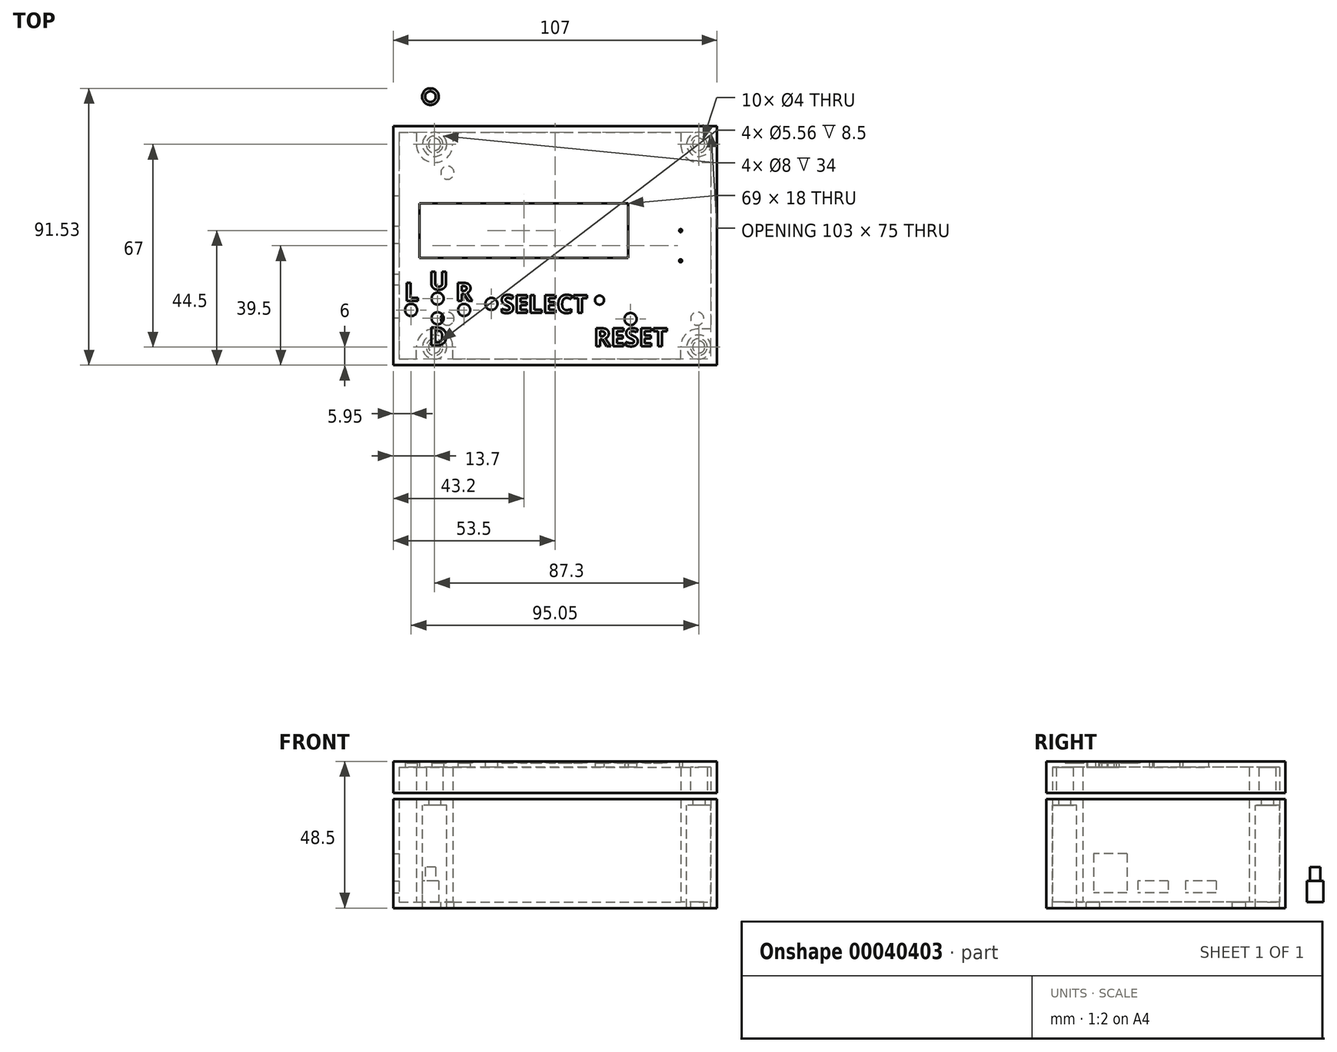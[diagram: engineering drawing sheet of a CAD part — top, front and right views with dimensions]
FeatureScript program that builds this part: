
annotation { "Feature Type Name" : "Feature", "Feature Type Description" : "" }
export const myFeature = defineFeature(function(context is Context, id is Id, definition is map)
    precondition{}
    {
        {
            assignVariable(context, id + "F0", {"name" : "Wall_T", "anyValue" : 2});
        }
        {
            var Q0;
            Q0=qCreatedBy(makeId("Top.planeOp"),FACE);
            var sketch = newSketch(context, id + "F1", { "sketchPlane" : qUnion([Q0])});
            skLineSegment(sketch, "E0.bottom", {"start": v(-50.8, 26.67) * mm, "end": v(50.8, 26.67) * mm});
            skLineSegment(sketch, "E0.top", {"start": v(-50.8, -26.67) * mm, "end": v(50.8, -26.67) * mm});
            skLineSegment(sketch, "E0.left", {"start": v(-50.8, 26.67) * mm, "end": v(-50.8, -26.67) * mm});
            skLineSegment(sketch, "E0.right", {"start": v(50.8, 26.67) * mm, "end": v(50.8, -26.67) * mm});
            skPoint(sketch, "E1", {"position": v(0, 26.67) * mm});
            skPoint(sketch, "E2", {"position": v(50.8, 0) * mm});
            skLineSegment(sketch, "E3.bottom", {"start": v(-50.8, -13.87) * mm, "end": v(-52.8, -13.87) * mm});
            skLineSegment(sketch, "E3.top", {"start": v(-50.8, -22.87) * mm, "end": v(-52.8, -22.87) * mm});
            skLineSegment(sketch, "E3.left", {"start": v(-50.8, -13.87) * mm, "end": v(-50.8, -22.87) * mm});
            skLineSegment(sketch, "E3.right", {"start": v(-52.8, -13.87) * mm, "end": v(-52.8, -22.87) * mm});
            skLineSegment(sketch, "E4.bottom", {"start": v(-50.8, -0.27) * mm, "end": v(-52.3, -0.27) * mm});
            skLineSegment(sketch, "E4.top", {"start": v(-50.8, -8.37) * mm, "end": v(-52.3, -8.37) * mm});
            skLineSegment(sketch, "E4.left", {"start": v(-50.8, -0.27) * mm, "end": v(-50.8, -8.37) * mm});
            skLineSegment(sketch, "E4.right", {"start": v(-52.3, -0.27) * mm, "end": v(-52.3, -8.37) * mm});
            skLineSegment(sketch, "E5.bottom", {"start": v(-50.8, 15.58) * mm, "end": v(-52.3, 15.58) * mm});
            skLineSegment(sketch, "E5.top", {"start": v(-50.8, 7.48) * mm, "end": v(-52.3, 7.48) * mm});
            skLineSegment(sketch, "E5.left", {"start": v(-50.8, 15.58) * mm, "end": v(-50.8, 7.48) * mm});
            skLineSegment(sketch, "E5.right", {"start": v(-52.3, 15.58) * mm, "end": v(-52.3, 7.48) * mm});
            skCircle(sketch, "E6", {"center": v(-35.56, 24.13) * mm, "radius": 0.64 * mm});
            skCircle(sketch, "E7", {"center": v(-35.56, -24.13) * mm, "radius": 0.64 * mm});
            skCircle(sketch, "E8", {"center": v(39.37, 24.13) * mm, "radius": 0.64 * mm});
            skCircle(sketch, "E9", {"center": v(15.24, 8.9) * mm, "radius": 0.64 * mm});
            skCircle(sketch, "E10", {"center": v(15.24, -19.05) * mm, "radius": 0.64 * mm});
            skCircle(sketch, "E11", {"center": v(47, -24.13) * mm, "radius": 0.64 * mm});
            skCircle(sketch, "E12", {"center": v(-44.8, 22.17) * mm, "radius": 1.5 * mm});
            skSolve(sketch);
        }
        {
            var Q0;
            Q0=qCreatedBy(makeId("Top.planeOp"),FACE);
            var sketch = newSketch(context, id + "F2", { "sketchPlane" : qUnion([Q0])});
            skLineSegment(sketch, "E13.bottom", {"start": v(-50.8, 28) * mm, "end": v(30.2, 28) * mm});
            skLineSegment(sketch, "E13.top", {"start": v(-50.8, -28) * mm, "end": v(30.2, -28) * mm});
            skLineSegment(sketch, "E13.left", {"start": v(-50.8, 28) * mm, "end": v(-50.8, -28) * mm});
            skLineSegment(sketch, "E13.right", {"start": v(30.2, 28) * mm, "end": v(30.2, -28) * mm});
            skPoint(sketch, "E14", {"position": v(30.2, 0) * mm});
            skLineSegment(sketch, "E15.bottom", {"start": v(-44.8, 14) * mm, "end": v(24.2, 14) * mm});
            skLineSegment(sketch, "E15.top", {"start": v(-44.8, -4) * mm, "end": v(24.2, -4) * mm});
            skLineSegment(sketch, "E15.left", {"start": v(-44.8, 14) * mm, "end": v(-44.8, -4) * mm});
            skLineSegment(sketch, "E15.right", {"start": v(24.2, 14) * mm, "end": v(24.2, -4) * mm});
            skCircle(sketch, "E16", {"center": v(-47.55, -21.25) * mm, "radius": 2 * mm});
            skCircle(sketch, "E17", {"center": v(-38.8, -17.5) * mm, "radius": 2 * mm});
            skCircle(sketch, "E18", {"center": v(-38.8, -24) * mm, "radius": 2 * mm});
            skCircle(sketch, "E19", {"center": v(-30.05, -21.25) * mm, "radius": 2 * mm});
            skCircle(sketch, "E20", {"center": v(-21.05, -19.25) * mm, "radius": 2 * mm});
            skCircle(sketch, "E21", {"center": v(24.95, -24.25) * mm, "radius": 2 * mm});
            skCircle(sketch, "E22", {"center": v(14.7, -18) * mm, "radius": 1.5 * mm});
            skSolve(sketch);
        }
        {
            var Q0;
            Q0=qCreatedBy(makeId("Top.planeOp"),FACE);
            var sketch = newSketch(context, id + "F3", { "sketchPlane" : qUnion([Q0])});
            skLineSegment(sketch, "E23.bottom", {"start": v(-51.5, 37.5) * mm, "end": v(51.5, 37.5) * mm});
            skLineSegment(sketch, "E23.top", {"start": v(-51.5, -37.5) * mm, "end": v(51.5, -37.5) * mm});
            skLineSegment(sketch, "E23.left", {"start": v(-51.5, 37.5) * mm, "end": v(-51.5, -37.5) * mm});
            skLineSegment(sketch, "E23.right", {"start": v(51.5, 37.5) * mm, "end": v(51.5, -37.5) * mm});
            skPoint(sketch, "E24", {"position": v(0, 37.5) * mm});
            skLineSegment(sketch, "E25.bottom", {"start": v(-53.5, 39.5) * mm, "end": v(53.5, 39.5) * mm});
            skLineSegment(sketch, "E25.top", {"start": v(-53.5, -39.5) * mm, "end": v(53.5, -39.5) * mm});
            skLineSegment(sketch, "E25.left", {"start": v(-53.5, 39.5) * mm, "end": v(-53.5, -39.5) * mm});
            skLineSegment(sketch, "E25.right", {"start": v(53.5, 39.5) * mm, "end": v(53.5, -39.5) * mm});
            skPoint(sketch, "E26", {"position": v(0, 39.5) * mm});
            skPoint(sketch, "E27", {"position": v(51.5, 0) * mm});
            skPoint(sketch, "E28", {"position": v(53.5, 0) * mm});
            skLineSegment(sketch, "E29.bottom", {"start": v(-53.5, -12.87) * mm, "end": v(-51.5, -12.87) * mm});
            skLineSegment(sketch, "E29.top", {"start": v(-53.5, -23.87) * mm, "end": v(-51.5, -23.87) * mm});
            skLineSegment(sketch, "E29.left", {"start": v(-53.5, -12.87) * mm, "end": v(-53.5, -23.87) * mm});
            skLineSegment(sketch, "E29.right", {"start": v(-51.5, -12.87) * mm, "end": v(-51.5, -23.87) * mm});
            skLineSegment(sketch, "E30.bottom", {"start": v(-53.5, 0.73) * mm, "end": v(-51.5, 0.73) * mm});
            skLineSegment(sketch, "E30.top", {"start": v(-53.5, -9.37) * mm, "end": v(-51.5, -9.37) * mm});
            skLineSegment(sketch, "E30.left", {"start": v(-53.5, 0.73) * mm, "end": v(-53.5, -9.37) * mm});
            skLineSegment(sketch, "E30.right", {"start": v(-51.5, 0.73) * mm, "end": v(-51.5, -9.37) * mm});
            skLineSegment(sketch, "E31.bottom", {"start": v(-53.5, 16.58) * mm, "end": v(-51.5, 16.58) * mm});
            skLineSegment(sketch, "E31.top", {"start": v(-53.5, 6.48) * mm, "end": v(-51.5, 6.48) * mm});
            skLineSegment(sketch, "E31.left", {"start": v(-53.5, 16.58) * mm, "end": v(-53.5, 6.48) * mm});
            skLineSegment(sketch, "E31.right", {"start": v(-51.5, 16.58) * mm, "end": v(-51.5, 6.48) * mm});
            skCircle(sketch, "E32", {"center": v(-35.56, -24.13) * mm, "radius": 2.18 * mm});
            skCircle(sketch, "E33", {"center": v(-35.56, 24.13) * mm, "radius": 2.18 * mm});
            skCircle(sketch, "E34", {"center": v(47, -24.13) * mm, "radius": 2.18 * mm});
            skCircle(sketch, "E35", {"center": v(47.5, 33.5) * mm, "radius": 4 * mm});
            skArc(sketch, "E36", {"start": v(41.5, 33.5) * mm, "mid": v(43.26, 29.26) * mm, "end": v(47.5, 27.5) * mm});
            skLineSegment(sketch, "E37", {"start": v(41.5, 33.5) * mm, "end": v(47.5, 33.5) * mm, "construction": true});
            skLineSegment(sketch, "E38", {"start": v(47.5, 27.5) * mm, "end": v(47.5, 33.5) * mm, "construction": true});
            skLineSegment(sketch, "E39", {"start": v(41.5, 33.5) * mm, "end": v(41.5, 37.5) * mm});
            skLineSegment(sketch, "E40", {"start": v(47.5, 27.5) * mm, "end": v(51.5, 27.5) * mm});
            skArc(sketch, "E41", {"start": v(47.5, -27.5) * mm, "mid": v(43.26, -29.26) * mm, "end": v(41.5, -33.5) * mm});
            skCircle(sketch, "E42", {"center": v(47.5, -33.5) * mm, "radius": 4 * mm});
            skLineSegment(sketch, "E43", {"start": v(47.5, -27.5) * mm, "end": v(51.5, -27.5) * mm});
            skLineSegment(sketch, "E44", {"start": v(47.5, -27.5) * mm, "end": v(47.5, -33.5) * mm, "construction": true});
            skLineSegment(sketch, "E45", {"start": v(41.5, -33.5) * mm, "end": v(47.5, -33.5) * mm, "construction": true});
            skLineSegment(sketch, "E46", {"start": v(41.5, -33.5) * mm, "end": v(41.5, -37.5) * mm});
            skCircle(sketch, "E47", {"center": v(-39.8, -33.5) * mm, "radius": 4 * mm});
            skArc(sketch, "E48", {"start": v(-33.8, -33.5) * mm, "mid": v(-39.8, -27.5) * mm, "end": v(-45.8, -33.5) * mm});
            skLineSegment(sketch, "E49", {"start": v(-45.8, -33.5) * mm, "end": v(-39.8, -33.5) * mm, "construction": true});
            skLineSegment(sketch, "E50", {"start": v(-33.8, -33.5) * mm, "end": v(-39.8, -33.5) * mm, "construction": true});
            skLineSegment(sketch, "E51", {"start": v(-33.8, -33.5) * mm, "end": v(-33.8, -37.5) * mm});
            skCircle(sketch, "E52", {"center": v(-39.8, 33.5) * mm, "radius": 4 * mm});
            skArc(sketch, "E53", {"start": v(-45.8, 33.5) * mm, "mid": v(-39.8, 27.5) * mm, "end": v(-33.8, 33.5) * mm});
            skLineSegment(sketch, "E54", {"start": v(-33.8, 33.5) * mm, "end": v(-39.8, 33.5) * mm, "construction": true});
            skLineSegment(sketch, "E55", {"start": v(-45.8, 33.5) * mm, "end": v(-39.8, 33.5) * mm, "construction": true});
            skLineSegment(sketch, "E56", {"start": v(-33.8, 33.5) * mm, "end": v(-33.8, 37.5) * mm});
            skLineSegment(sketch, "E57", {"start": v(-45.8, -33.5) * mm, "end": v(-45.8, -37.5) * mm});
            skLineSegment(sketch, "E58", {"start": v(-45.8, 33.5) * mm, "end": v(-45.8, 37.5) * mm});
            skCircle(sketch, "E59", {"center": v(-39.8, 33.5) * mm, "radius": 2 * mm});
            skCircle(sketch, "E60", {"center": v(47.5, 33.5) * mm, "radius": 2 * mm});
            skCircle(sketch, "E61", {"center": v(47.5, -33.5) * mm, "radius": 2 * mm});
            skCircle(sketch, "E62", {"center": v(-39.8, -33.5) * mm, "radius": 2 * mm});
            skSolve(sketch);
        }
        {
            var Q0;
            {var subQ6=sQuery(id+"F3.wireOp",EDGE,"E23.bottom");Q0=makeQuery(id+"F3.imprint","IMPRINT",FACE,{"disambiguationData":[TD([[makeQuery(id+"F3.imprint","IMPRINT",EDGE,{"derivedFrom":subQ6}),1.0]])]});}
            var Q1;
            {var subQ1=sQuery(id+"F3.wireOp",EDGE,"E30.bottom");Q1=makeQuery(id+"F3.imprint","IMPRINT",FACE,{"disambiguationData":[TD([[makeQuery(id+"F3.imprint","IMPRINT",EDGE,{"derivedFrom":subQ1}),1.0]])]});}
            var Q2;
            {var subQ1=sQuery(id+"F3.wireOp",EDGE,"E29.bottom");Q2=makeQuery(id+"F3.imprint","IMPRINT",FACE,{"disambiguationData":[TD([[makeQuery(id+"F3.imprint","IMPRINT",EDGE,{"derivedFrom":subQ1}),1.0]])]});}
            var Q3;
            {var subQ5=sQuery(id+"F3.wireOp",EDGE,"E23.bottom");Q3=makeQuery(id+"F3.imprint","IMPRINT",FACE,{"disambiguationData":[TD([[makeQuery(id+"F3.imprint","IMPRINT",EDGE,{"derivedFrom":subQ5}),-1.0]])]});}
            var Q4;
            Q4=makeQuery(id+"F3.imprint","IMPRINT",FACE,{"disambiguationData":[TD([[makeQuery(id+"F3.imprint","IMPRINT",EDGE,{"derivedFrom":sQuery(id+"F3.wireOp",EDGE,"E31.bottom")}),-1.0]])]});
            var Q5;
            Q5=makeQuery(id+"F3.imprint","IMPRINT",FACE,{"disambiguationData":[TD([[makeQuery(id+"F3.imprint","IMPRINT",EDGE,{"derivedFrom":sQuery(id+"F3.wireOp",EDGE,"E30.bottom")}),-1.0]])]});
            var Q6;
            Q6=makeQuery(id+"F3.imprint","IMPRINT",FACE,{"disambiguationData":[TD([[makeQuery(id+"F3.imprint","IMPRINT",EDGE,{"derivedFrom":sQuery(id+"F3.wireOp",EDGE,"E29.bottom")}),-1.0]])]});
            var Q7;
            {var subQ2=sQuery(id+"F3.wireOp",EDGE,"E29.right");Q7=makeQuery(id+"F3.imprint","IMPRINT",FACE,{"disambiguationData":[TD([[makeQuery(id+"F3.imprint","IMPRINT",EDGE,{"derivedFrom":subQ2}),1.0]])]});}
            var Q8;
            {var subQ0=sQuery(id+"F3.wireOp",EDGE,"E51");Q8=makeQuery(id+"F3.imprint","IMPRINT",FACE,{"disambiguationData":[TD([[makeQuery(id+"F3.imprint","IMPRINT",EDGE,{"derivedFrom":subQ0}),-1.0]])]});}
            var Q9;
            {var subQ0=sQuery(id+"F3.wireOp",EDGE,"E57");Q9=makeQuery(id+"F3.imprint","IMPRINT",FACE,{"disambiguationData":[TD([[makeQuery(id+"F3.imprint","IMPRINT",EDGE,{"derivedFrom":subQ0}),1.0]])]});}
            var Q10;
            {var subQ1=sQuery(id+"F3.wireOp",EDGE,"e28c1a44-09c7-43ad-9793-d904d9dc9239");var subQ3=sQuery(id+"F3.wireOp",EDGE,"E23.top");var subQ5=makeQuery(id+"F3.imprint","INTERSECT",VERTEX,{"derivedFrom":[subQ3,subQ1]});Q10=makeQuery(id+"F3.imprint","IMPRINT",FACE,{"disambiguationData":[TD([[makeQuery(id+"F3.imprint","IMPRINT",EDGE,{"disambiguationData":[TD([[subQ5,-1.0]])],"derivedFrom":subQ3}),1.0]])]});}
            var Q11;
            Q11=makeQuery(id+"F3.imprint","IMPRINT",FACE,{"disambiguationData":[TD([[makeQuery(id+"F3.imprint","IMPRINT",EDGE,{"derivedFrom":sQuery(id+"F3.wireOp",EDGE,"E32")}),-1.0]])]});
            var Q12;
            {var subQ0=sQuery(id+"F3.wireOp",EDGE,"E56");Q12=makeQuery(id+"F3.imprint","IMPRINT",FACE,{"disambiguationData":[TD([[makeQuery(id+"F3.imprint","IMPRINT",EDGE,{"derivedFrom":subQ0}),1.0]])]});}
            var Q13;
            Q13=makeQuery(id+"F3.imprint","IMPRINT",FACE,{"disambiguationData":[TD([[makeQuery(id+"F3.imprint","IMPRINT",EDGE,{"derivedFrom":sQuery(id+"F3.wireOp",EDGE,"E36")}),1.0]])]});
            var Q14;
            Q14=makeQuery(id+"F3.imprint","IMPRINT",FACE,{"disambiguationData":[TD([[makeQuery(id+"F3.imprint","IMPRINT",EDGE,{"derivedFrom":sQuery(id+"F3.wireOp",EDGE,"E41")}),1.0]])]});
            var Q15;
            {var subQ1=sQuery(id+"F3.wireOp",EDGE,"E23.right");var subQ3=sQuery(id+"F3.wireOp",EDGE,"E23.top");var subQ5=makeQuery(id+"F3.imprint","INTERSECT",VERTEX,{"derivedFrom":[subQ3,subQ1]});Q15=makeQuery(id+"F3.imprint","IMPRINT",FACE,{"disambiguationData":[TD([[makeQuery(id+"F3.imprint","IMPRINT",EDGE,{"disambiguationData":[TD([[subQ5,1.0]])],"derivedFrom":subQ3}),1.0]])]});}
            var Q16;
            {var subQ0=sQuery(id+"F3.wireOp",EDGE,"E58");Q16=makeQuery(id+"F3.imprint","IMPRINT",FACE,{"disambiguationData":[TD([[makeQuery(id+"F3.imprint","IMPRINT",EDGE,{"derivedFrom":subQ0}),-1.0]])]});}
            var Q17;
            {var subQ0=sQuery(id+"F3.wireOp",EDGE,"E23.right");var subQ1=sQuery(id+"F3.wireOp",EDGE,"E23.bottom");var subQ2=makeQuery(id+"F3.imprint","INTERSECT",VERTEX,{"derivedFrom":[subQ1,subQ0]});Q17=makeQuery(id+"F3.imprint","IMPRINT",FACE,{"disambiguationData":[TD([[makeQuery(id+"F3.imprint","IMPRINT",EDGE,{"disambiguationData":[TD([[subQ2,1.0]])],"derivedFrom":subQ1}),-1.0]])]});}
            extrude(context, id + "F4", {"entities" : qUnion([Q0, Q1, Q2, Q3, Q4, Q5, Q6, Q7, Q8, Q9, Q10, Q11, Q12, Q13, Q14, Q15, Q16, Q17]), "oppositeDirection" : true, "depth" : (getVariable(context, 'Wall_T')) * mm});
        }
        {
            var Q0;
            {var subQ30=sQuery(id+"F3.wireOp",EDGE,"E25.bottom");Q0=makeQuery(id+"F3.imprint","IMPRINT",FACE,{"disambiguationData":[TD([[makeQuery(id+"F3.imprint","IMPRINT",EDGE,{"derivedFrom":subQ30}),-1.0]])]});}
            var Q1;
            {var subQ1=sQuery(id+"F3.wireOp",EDGE,"E29.bottom");Q1=makeQuery(id+"F3.imprint","IMPRINT",FACE,{"disambiguationData":[TD([[makeQuery(id+"F3.imprint","IMPRINT",EDGE,{"derivedFrom":subQ1}),1.0]])]});}
            var Q2;
            {var subQ1=sQuery(id+"F3.wireOp",EDGE,"E30.bottom");Q2=makeQuery(id+"F3.imprint","IMPRINT",FACE,{"disambiguationData":[TD([[makeQuery(id+"F3.imprint","IMPRINT",EDGE,{"derivedFrom":subQ1}),1.0]])]});}
            var Q3;
            {var subQ0=sQuery(id+"F3.wireOp",EDGE,"E58");Q3=makeQuery(id+"F3.imprint","IMPRINT",FACE,{"disambiguationData":[TD([[makeQuery(id+"F3.imprint","IMPRINT",EDGE,{"derivedFrom":subQ0}),-1.0]])]});}
            var Q4;
            {var subQ1=sQuery(id+"F3.wireOp",EDGE,"e28c1a44-09c7-43ad-9793-d904d9dc9239");var subQ3=sQuery(id+"F3.wireOp",EDGE,"E23.bottom");var subQ5=makeQuery(id+"F3.imprint","INTERSECT",VERTEX,{"derivedFrom":[subQ3,subQ1]});Q4=makeQuery(id+"F3.imprint","IMPRINT",FACE,{"disambiguationData":[TD([[makeQuery(id+"F3.imprint","IMPRINT",EDGE,{"disambiguationData":[TD([[subQ5,-1.0]])],"derivedFrom":subQ3}),-1.0]])]});}
            var Q5;
            {var subQ0=sQuery(id+"F3.wireOp",EDGE,"E56");Q5=makeQuery(id+"F3.imprint","IMPRINT",FACE,{"disambiguationData":[TD([[makeQuery(id+"F3.imprint","IMPRINT",EDGE,{"derivedFrom":subQ0}),1.0]])]});}
            var Q6;
            Q6=makeQuery(id+"F3.imprint","IMPRINT",FACE,{"disambiguationData":[TD([[makeQuery(id+"F3.imprint","IMPRINT",EDGE,{"derivedFrom":sQuery(id+"F3.wireOp",EDGE,"E36")}),1.0]])]});
            var Q7;
            {var subQ1=sQuery(id+"F3.wireOp",EDGE,"E23.right");var subQ3=sQuery(id+"F3.wireOp",EDGE,"E23.bottom");var subQ5=makeQuery(id+"F3.imprint","INTERSECT",VERTEX,{"derivedFrom":[subQ3,subQ1]});Q7=makeQuery(id+"F3.imprint","IMPRINT",FACE,{"disambiguationData":[TD([[makeQuery(id+"F3.imprint","IMPRINT",EDGE,{"disambiguationData":[TD([[subQ5,1.0]])],"derivedFrom":subQ3}),-1.0]])]});}
            var Q8;
            {var subQ0=sQuery(id+"F3.wireOp",EDGE,"E51");Q8=makeQuery(id+"F3.imprint","IMPRINT",FACE,{"disambiguationData":[TD([[makeQuery(id+"F3.imprint","IMPRINT",EDGE,{"derivedFrom":subQ0}),-1.0]])]});}
            var Q9;
            {var subQ1=sQuery(id+"F3.wireOp",EDGE,"e28c1a44-09c7-43ad-9793-d904d9dc9239");var subQ3=sQuery(id+"F3.wireOp",EDGE,"E23.top");var subQ5=makeQuery(id+"F3.imprint","INTERSECT",VERTEX,{"derivedFrom":[subQ3,subQ1]});Q9=makeQuery(id+"F3.imprint","IMPRINT",FACE,{"disambiguationData":[TD([[makeQuery(id+"F3.imprint","IMPRINT",EDGE,{"disambiguationData":[TD([[subQ5,-1.0]])],"derivedFrom":subQ3}),1.0]])]});}
            var Q10;
            {var subQ0=sQuery(id+"F3.wireOp",EDGE,"E57");Q10=makeQuery(id+"F3.imprint","IMPRINT",FACE,{"disambiguationData":[TD([[makeQuery(id+"F3.imprint","IMPRINT",EDGE,{"derivedFrom":subQ0}),1.0]])]});}
            var Q11;
            {var subQ1=sQuery(id+"F3.wireOp",EDGE,"E23.right");var subQ3=sQuery(id+"F3.wireOp",EDGE,"E23.top");var subQ5=makeQuery(id+"F3.imprint","INTERSECT",VERTEX,{"derivedFrom":[subQ3,subQ1]});Q11=makeQuery(id+"F3.imprint","IMPRINT",FACE,{"disambiguationData":[TD([[makeQuery(id+"F3.imprint","IMPRINT",EDGE,{"disambiguationData":[TD([[subQ5,1.0]])],"derivedFrom":subQ3}),1.0]])]});}
            var Q12;
            Q12=makeQuery(id+"F3.imprint","IMPRINT",FACE,{"disambiguationData":[TD([[makeQuery(id+"F3.imprint","IMPRINT",EDGE,{"derivedFrom":sQuery(id+"F3.wireOp",EDGE,"E41")}),1.0]])]});
            var Q13;
            Q13=makeQuery(id+"F3.imprint","IMPRINT",FACE,{"disambiguationData":[TD([[makeQuery(id+"F3.imprint","IMPRINT",EDGE,{"derivedFrom":sQuery(id+"F3.wireOp",EDGE,"E31.bottom")}),-1.0]])]});
            var Q14;
            Q14=makeQuery(id+"F3.imprint","IMPRINT",FACE,{"disambiguationData":[TD([[makeQuery(id+"F3.imprint","IMPRINT",EDGE,{"derivedFrom":sQuery(id+"F3.wireOp",EDGE,"E30.bottom")}),-1.0]])]});
            var Q15;
            Q15=makeQuery(id+"F3.imprint","IMPRINT",FACE,{"disambiguationData":[TD([[makeQuery(id+"F3.imprint","IMPRINT",EDGE,{"derivedFrom":sQuery(id+"F3.wireOp",EDGE,"E29.bottom")}),-1.0]])]});
            extrude(context, id + "F5", {"entities" : qUnion([Q0, Q1, Q2, Q3, Q4, Q5, Q6, Q7, Q8, Q9, Q10, Q11, Q12, Q13, Q14, Q15]), "operationType" : NewBodyOperationType.ADD, "depth" : 34 * mm});
        }
        {
            var Q0;
            Q0=makeQuery(id+"F3.imprint","IMPRINT",FACE,{"disambiguationData":[TD([[makeQuery(id+"F3.imprint","IMPRINT",EDGE,{"derivedFrom":sQuery(id+"F3.wireOp",EDGE,"E31.bottom")}),-1.0]])]});
            var Q1;
            Q1=makeQuery(id+"F3.imprint","IMPRINT",FACE,{"disambiguationData":[TD([[makeQuery(id+"F3.imprint","IMPRINT",EDGE,{"derivedFrom":sQuery(id+"F3.wireOp",EDGE,"E30.bottom")}),-1.0]])]});
            extrude(context, id + "F6", {"entities" : qUnion([Q0, Q1]), "operationType" : NewBodyOperationType.REMOVE, "depth" : 7 * mm, "hasSecondDirection" : true, "secondDirectionOppositeDirection" : false, "secondDirectionDepth" : 3 * mm});
        }
        {
            var Q0;
            Q0=makeQuery(id+"F3.imprint","IMPRINT",FACE,{"disambiguationData":[TD([[makeQuery(id+"F3.imprint","IMPRINT",EDGE,{"derivedFrom":sQuery(id+"F3.wireOp",EDGE,"E29.bottom")}),-1.0]])]});
            var Q1;
            Q1=makeQuery(id+"F6.opExtrude","CAP_FACE",FACE,{"disambiguationData":[OSD([sQuery(id+"F3.wireOp",EDGE,"E31.bottom"),sQuery(id+"F3.wireOp",EDGE,"E31.top"),sQuery(id+"F3.wireOp",EDGE,"E31.left"),sQuery(id+"F3.wireOp",EDGE,"E31.right")])],"isStart":false});
            var Q2;
            {var subQ0=sQuery(id+"F3.wireOp",EDGE,"E23.bottom");var subQ1=sQuery(id+"F3.wireOp",EDGE,"E23.top");var subQ2=sQuery(id+"F3.wireOp",EDGE,"E25.bottom");var subQ3=sQuery(id+"F3.wireOp",EDGE,"E25.top");var subQ4=sQuery(id+"F3.wireOp",EDGE,"E25.left");var subQ5=sQuery(id+"F3.wireOp",EDGE,"E29.left");var subQ6=sQuery(id+"F3.wireOp",EDGE,"E30.left");var subQ7=sQuery(id+"F3.wireOp",EDGE,"E31.left");var subQ8=sQuery(id+"F3.wireOp",EDGE,"e28c1a44-09c7-43ad-9793-d904d9dc9239");var subQ9=sQuery(id+"F3.wireOp",EDGE,"E48");var subQ10=sQuery(id+"F3.wireOp",EDGE,"E53");var subQ17=sQuery(id+"F3.wireOp",EDGE,"E29.bottom");Q2=makeQuery(id+"FmseZqoOlNMf1UM_2.boolean.opBoolean","SPLIT",FACE,{"disambiguationData":[TD([makeQuery(id+"F5.opExtrude","SWEPT_FACE",FACE,{"disambiguationData":[OSD([subQ17])]})])],"derivedFrom":makeQuery(id+"FmseZqoOlNMf1UM_2.opExtrude","CAP_FACE",FACE,{"disambiguationData":[OSD([subQ0,subQ1,sQuery(id+"F3.wireOp",EDGE,"E23.right"),subQ2,subQ3,subQ4,sQuery(id+"F3.wireOp",EDGE,"E25.right"),subQ5,subQ6,subQ7,subQ8,sQuery(id+"F3.wireOp",EDGE,"E36"),sQuery(id+"F3.wireOp",EDGE,"E39"),sQuery(id+"F3.wireOp",EDGE,"E40"),sQuery(id+"F3.wireOp",EDGE,"E41"),sQuery(id+"F3.wireOp",EDGE,"E43"),sQuery(id+"F3.wireOp",EDGE,"E46"),subQ9,sQuery(id+"F3.wireOp",EDGE,"E51"),subQ10,sQuery(id+"F3.wireOp",EDGE,"E56"),sQuery(id+"F3.wireOp",EDGE,"E59"),sQuery(id+"F3.wireOp",EDGE,"E60"),sQuery(id+"F3.wireOp",EDGE,"E61"),sQuery(id+"F3.wireOp",EDGE,"E62")])],"isStart":true})});}
            extrude(context, id + "F7", {"entities" : qUnion([Q0]), "operationType" : NewBodyOperationType.REMOVE, "endBoundEntityFace" : qUnion([Q1]), "depth" : 16 * mm, "hasSecondDirection" : true, "secondDirectionOppositeDirection" : false, "secondDirectionBoundEntityFace" : qUnion([Q2]), "secondDirectionDepth" : 3 * mm});
        }
        {
            var Q0;
            Q0=makeQuery(id+"F3.imprint","IMPRINT",FACE,{"disambiguationData":[TD([[makeQuery(id+"F3.imprint","IMPRINT",EDGE,{"derivedFrom":sQuery(id+"F3.wireOp",EDGE,"E52")}),1.0]])]});
            var Q1;
            Q1=makeQuery(id+"F3.imprint","IMPRINT",FACE,{"disambiguationData":[TD([[makeQuery(id+"F3.imprint","IMPRINT",EDGE,{"derivedFrom":sQuery(id+"F3.wireOp",EDGE,"E47")}),1.0]])]});
            var Q2;
            Q2=makeQuery(id+"F3.imprint","IMPRINT",FACE,{"disambiguationData":[TD([[makeQuery(id+"F3.imprint","IMPRINT",EDGE,{"derivedFrom":sQuery(id+"F3.wireOp",EDGE,"E60")}),-1.0]])]});
            var Q3;
            Q3=makeQuery(id+"F3.imprint","IMPRINT",FACE,{"disambiguationData":[TD([[makeQuery(id+"F3.imprint","IMPRINT",EDGE,{"derivedFrom":sQuery(id+"F3.wireOp",EDGE,"E61")}),-1.0]])]});
            extrude(context, id + "F8", {"entities" : qUnion([Q0, Q1, Q2, Q3]), "operationType" : NewBodyOperationType.ADD, "depth" : 34 * mm, "hasSecondDirection" : true, "secondDirectionOppositeDirection" : false, "secondDirectionDepth" : 32 * mm});
        }
        {
            var Q0;
            Q0=qCreatedBy(makeId("Top.planeOp"),FACE);
            var sketch = newSketch(context, id + "F9", { "sketchPlane" : qUnion([Q0])});
            skCircle(sketch, "E63", {"center": v(41.5, 5) * mm, "radius": 0.5 * mm});
            skCircle(sketch, "E64", {"center": v(41.5, -5) * mm, "radius": 0.5 * mm});
            skLineSegment(sketch, "E65.bottom", {"start": v(-51.5, 37.5) * mm, "end": v(51.5, 37.5) * mm});
            skLineSegment(sketch, "E65.top", {"start": v(-51.5, -37.5) * mm, "end": v(51.5, -37.5) * mm});
            skLineSegment(sketch, "E65.left", {"start": v(-51.5, 37.5) * mm, "end": v(-51.5, -37.5) * mm});
            skLineSegment(sketch, "E65.right", {"start": v(51.5, 37.5) * mm, "end": v(51.5, -37.5) * mm});
            skLineSegment(sketch, "E66.bottom", {"start": v(-53.5, 39.5) * mm, "end": v(53.5, 39.5) * mm});
            skLineSegment(sketch, "E66.top", {"start": v(-53.5, -39.5) * mm, "end": v(53.5, -39.5) * mm});
            skLineSegment(sketch, "E66.left", {"start": v(-53.5, 39.5) * mm, "end": v(-53.5, -39.5) * mm});
            skLineSegment(sketch, "E66.right", {"start": v(53.5, 39.5) * mm, "end": v(53.5, -39.5) * mm});
            skLineSegment(sketch, "E67", {"start": v(41.5, 5) * mm, "end": v(41.5, -5) * mm, "construction": true});
            skPoint(sketch, "E68", {"position": v(41.5, 0) * mm});
            skCircle(sketch, "E69", {"center": v(-39.8, 33.5) * mm, "radius": 2.78 * mm});
            skLineSegment(sketch, "E70", {"start": v(-45.8, 37.5) * mm, "end": v(-45.8, 33.5) * mm});
            skLineSegment(sketch, "E71", {"start": v(-33.8, 37.5) * mm, "end": v(-33.8, 33.5) * mm});
            skArc(sketch, "E72", {"start": v(-45.8, 33.5) * mm, "mid": v(-39.8, 27.5) * mm, "end": v(-33.8, 33.5) * mm});
            skLineSegment(sketch, "E73", {"start": v(41.5, 37.5) * mm, "end": v(41.5, 33.5) * mm});
            skLineSegment(sketch, "E74", {"start": v(51.5, 27.5) * mm, "end": v(47.5, 27.5) * mm});
            skLineSegment(sketch, "E75", {"start": v(51.5, -27.5) * mm, "end": v(47.5, -27.5) * mm});
            skLineSegment(sketch, "E76", {"start": v(41.5, -37.5) * mm, "end": v(41.5, -33.5) * mm});
            skLineSegment(sketch, "E77", {"start": v(-33.8, -37.5) * mm, "end": v(-33.8, -33.5) * mm});
            skLineSegment(sketch, "E78", {"start": v(-45.8, -37.5) * mm, "end": v(-45.8, -33.5) * mm});
            skArc(sketch, "E79", {"start": v(41.5, 33.5) * mm, "mid": v(43.26, 29.26) * mm, "end": v(47.5, 27.5) * mm});
            skArc(sketch, "E80", {"start": v(41.5, -33.5) * mm, "mid": v(43.26, -29.26) * mm, "end": v(47.5, -27.5) * mm});
            skArc(sketch, "E81", {"start": v(-45.8, -33.5) * mm, "mid": v(-39.8, -27.5) * mm, "end": v(-33.8, -33.5) * mm});
            skCircle(sketch, "E82", {"center": v(47.5, 33.5) * mm, "radius": 2.78 * mm});
            skCircle(sketch, "E83", {"center": v(47.5, -33.5) * mm, "radius": 2.78 * mm});
            skCircle(sketch, "E84", {"center": v(-39.8, -33.5) * mm, "radius": 2.78 * mm});
            skText(sketch, "E85", { "text": "RESET", "fontName": "OpenSans-Bold.ttf"});
            skText(sketch, "E86", { "text": "SELECT", "fontName": "OpenSans-Bold.ttf"});
            skPoint(sketch, "E87", {"position": v(-18.05, -19.25) * mm});
            skText(sketch, "E88", { "text": "U", "fontName": "OpenSans-Bold.ttf"});
            skText(sketch, "E89", { "text": "D", "fontName": "OpenSans-Bold.ttf"});
            skText(sketch, "E90", { "text": "L", "fontName": "OpenSans-Bold.ttf"});
            skText(sketch, "E91", { "text": "R", "fontName": "OpenSans-Bold.ttf"});
            const initialGuessF9  = {"E85": [0.0129, -0.03325, 1, 0, 0.006], "E86": [-0.01805, -0.02225, 1, 0, 0.006], "E88": [-0.0416, -0.0145, 1, 0, 0.006], "E89": [-0.04164, -0.033, 1, 0, 0.006], "E90": [-0.04976, -0.01825, 1, 0, 0.006], "E91": [-0.0328, -0.01825, 1, 0, 0.006]};
            skSetInitialGuess(sketch, initialGuessF9);
            skSolve(sketch);
        }
        {
            var Q0;
            Q0=makeQuery(id+"F9.imprint","IMPRINT",FACE,{"disambiguationData":[TD([[makeQuery(id+"F9.imprint","IMPRINT",EDGE,{"derivedFrom":sQuery(id+"F9.wireOp",EDGE,"E88.sketch_text.stroke-0")}),-1.0]])]});
            var Q1;
            Q1=makeQuery(id+"F9.imprint","IMPRINT",FACE,{"disambiguationData":[TD([[makeQuery(id+"F9.imprint","IMPRINT",EDGE,{"derivedFrom":sQuery(id+"F9.wireOp",EDGE,"E90.sketch_text.stroke-0")}),-1.0]])]});
            var Q2;
            Q2=makeQuery(id+"F9.imprint","IMPRINT",FACE,{"disambiguationData":[TD([[makeQuery(id+"F9.imprint","IMPRINT",EDGE,{"derivedFrom":sQuery(id+"F9.wireOp",EDGE,"E91.sketch_text.stroke-0")}),-1.0]])]});
            var Q3;
            Q3=makeQuery(id+"F9.imprint","IMPRINT",FACE,{"disambiguationData":[TD([[makeQuery(id+"F9.imprint","IMPRINT",EDGE,{"derivedFrom":sQuery(id+"F9.wireOp",EDGE,"E63")}),-1.0]])]});
            var Q4;
            Q4=makeQuery(id+"F9.imprint","IMPRINT",FACE,{"disambiguationData":[TD([[makeQuery(id+"F9.imprint","IMPRINT",EDGE,{"derivedFrom":sQuery(id+"F9.wireOp",EDGE,"E91.sketch_text.stroke-0")}),1.0]])]});
            var Q5;
            Q5=makeQuery(id+"F9.imprint","IMPRINT",FACE,{"disambiguationData":[TD([[makeQuery(id+"F9.imprint","IMPRINT",EDGE,{"derivedFrom":sQuery(id+"F9.wireOp",EDGE,"E86.sketch_text.stroke-0")}),-1.0]])]});
            var Q6;
            Q6=makeQuery(id+"F9.imprint","IMPRINT",FACE,{"disambiguationData":[TD([[makeQuery(id+"F9.imprint","IMPRINT",EDGE,{"derivedFrom":sQuery(id+"F9.wireOp",EDGE,"E86.sketch_text.stroke-28")}),-1.0]])]});
            var Q7;
            Q7=makeQuery(id+"F9.imprint","IMPRINT",FACE,{"disambiguationData":[TD([[makeQuery(id+"F9.imprint","IMPRINT",EDGE,{"derivedFrom":sQuery(id+"F9.wireOp",EDGE,"E86.sketch_text.stroke-40")}),-1.0]])]});
            var Q8;
            Q8=makeQuery(id+"F9.imprint","IMPRINT",FACE,{"disambiguationData":[TD([[makeQuery(id+"F9.imprint","IMPRINT",EDGE,{"derivedFrom":sQuery(id+"F9.wireOp",EDGE,"E86.sketch_text.stroke-46")}),-1.0]])]});
            var Q9;
            Q9=makeQuery(id+"F9.imprint","IMPRINT",FACE,{"disambiguationData":[TD([[makeQuery(id+"F9.imprint","IMPRINT",EDGE,{"derivedFrom":sQuery(id+"F9.wireOp",EDGE,"E86.sketch_text.stroke-58")}),-1.0]])]});
            var Q10;
            Q10=makeQuery(id+"F9.imprint","IMPRINT",FACE,{"disambiguationData":[TD([[makeQuery(id+"F9.imprint","IMPRINT",EDGE,{"derivedFrom":sQuery(id+"F9.wireOp",EDGE,"E86.sketch_text.stroke-73")}),-1.0]])]});
            var Q11;
            Q11=makeQuery(id+"F9.imprint","IMPRINT",FACE,{"disambiguationData":[TD([[makeQuery(id+"F9.imprint","IMPRINT",EDGE,{"derivedFrom":sQuery(id+"F9.wireOp",EDGE,"E85.sketch_text.stroke-0")}),1.0]])]});
            var Q12;
            Q12=makeQuery(id+"F9.imprint","IMPRINT",FACE,{"disambiguationData":[TD([[makeQuery(id+"F9.imprint","IMPRINT",EDGE,{"derivedFrom":sQuery(id+"F9.wireOp",EDGE,"E85.sketch_text.stroke-0")}),-1.0]])]});
            var Q13;
            Q13=makeQuery(id+"F9.imprint","IMPRINT",FACE,{"disambiguationData":[TD([[makeQuery(id+"F9.imprint","IMPRINT",EDGE,{"derivedFrom":sQuery(id+"F9.wireOp",EDGE,"E85.sketch_text.stroke-19")}),-1.0]])]});
            var Q14;
            Q14=makeQuery(id+"F9.imprint","IMPRINT",FACE,{"disambiguationData":[TD([[makeQuery(id+"F9.imprint","IMPRINT",EDGE,{"derivedFrom":sQuery(id+"F9.wireOp",EDGE,"E85.sketch_text.stroke-31")}),-1.0]])]});
            var Q15;
            Q15=makeQuery(id+"F9.imprint","IMPRINT",FACE,{"disambiguationData":[TD([[makeQuery(id+"F9.imprint","IMPRINT",EDGE,{"derivedFrom":sQuery(id+"F9.wireOp",EDGE,"E85.sketch_text.stroke-59")}),-1.0]])]});
            var Q16;
            Q16=makeQuery(id+"F9.imprint","IMPRINT",FACE,{"disambiguationData":[TD([[makeQuery(id+"F9.imprint","IMPRINT",EDGE,{"derivedFrom":sQuery(id+"F9.wireOp",EDGE,"E85.sketch_text.stroke-71")}),-1.0]])]});
            var Q17;
            {var subQ1=sQuery(id+"F9.wireOp",EDGE,"E75");Q17=makeQuery(id+"F9.imprint","IMPRINT",FACE,{"disambiguationData":[TD([[makeQuery(id+"F9.imprint","IMPRINT",EDGE,{"derivedFrom":subQ1}),1.0]])]});}
            var Q18;
            Q18=makeQuery(id+"F9.imprint","IMPRINT",FACE,{"disambiguationData":[TD([[makeQuery(id+"F9.imprint","IMPRINT",EDGE,{"derivedFrom":sQuery(id+"F9.wireOp",EDGE,"E83")}),1.0]])]});
            var Q19;
            Q19=makeQuery(id+"F9.imprint","IMPRINT",FACE,{"disambiguationData":[TD([[makeQuery(id+"F9.imprint","IMPRINT",EDGE,{"derivedFrom":sQuery(id+"F9.wireOp",EDGE,"E69")}),1.0]])]});
            var Q20;
            Q20=makeQuery(id+"F9.imprint","IMPRINT",FACE,{"disambiguationData":[TD([[makeQuery(id+"F9.imprint","IMPRINT",EDGE,{"derivedFrom":sQuery(id+"F9.wireOp",EDGE,"E69")}),-1.0]])]});
            var Q21;
            {var subQ7=sQuery(id+"F9.wireOp",EDGE,"E65.left");Q21=makeQuery(id+"F9.imprint","IMPRINT",FACE,{"disambiguationData":[TD([[makeQuery(id+"F9.imprint","IMPRINT",EDGE,{"derivedFrom":subQ7}),-1.0]])]});}
            var Q22;
            Q22=makeQuery(id+"F9.imprint","IMPRINT",FACE,{"disambiguationData":[TD([[makeQuery(id+"F9.imprint","IMPRINT",EDGE,{"derivedFrom":sQuery(id+"F9.wireOp",EDGE,"E82")}),1.0]])]});
            var Q23;
            {var subQ1=sQuery(id+"F9.wireOp",EDGE,"E73");Q23=makeQuery(id+"F9.imprint","IMPRINT",FACE,{"disambiguationData":[TD([[makeQuery(id+"F9.imprint","IMPRINT",EDGE,{"derivedFrom":subQ1}),1.0]])]});}
            var Q24;
            {var subQ4=sQuery(id+"F9.wireOp",EDGE,"E89.sketch_text.stroke-7");Q24=makeQuery(id+"F9.imprint","IMPRINT",FACE,{"disambiguationData":[TD([[makeQuery(id+"F9.imprint","IMPRINT",EDGE,{"derivedFrom":subQ4}),1.0]])]});}
            var Q25;
            {var subQ5=sQuery(id+"F9.wireOp",EDGE,"E89.sketch_text.stroke-10");Q25=makeQuery(id+"F9.imprint","IMPRINT",FACE,{"disambiguationData":[TD([[makeQuery(id+"F9.imprint","IMPRINT",EDGE,{"derivedFrom":subQ5}),1.0]])]});}
            var Q26;
            {var subQ0=sQuery(id+"F9.wireOp",EDGE,"E89.sketch_text.stroke-2");Q26=makeQuery(id+"F9.imprint","IMPRINT",FACE,{"disambiguationData":[TD([[makeQuery(id+"F9.imprint","IMPRINT",EDGE,{"derivedFrom":subQ0}),-1.0]])]});}
            var Q27;
            {var subQ10=sQuery(id+"F9.wireOp",EDGE,"E89.sketch_text.stroke-0");Q27=makeQuery(id+"F9.imprint","IMPRINT",FACE,{"disambiguationData":[TD([[makeQuery(id+"F9.imprint","IMPRINT",EDGE,{"derivedFrom":subQ10}),-1.0]])]});}
            var Q28;
            {var subQ1=sQuery(id+"F9.wireOp",EDGE,"E89.sketch_text.stroke-4");Q28=makeQuery(id+"F9.imprint","IMPRINT",FACE,{"disambiguationData":[TD([[makeQuery(id+"F9.imprint","IMPRINT",EDGE,{"derivedFrom":subQ1}),-1.0]])]});}
            var Q29;
            {var subQ4=sQuery(id+"F9.wireOp",EDGE,"E77");Q29=makeQuery(id+"F9.imprint","IMPRINT",FACE,{"disambiguationData":[TD([[makeQuery(id+"F9.imprint","IMPRINT",EDGE,{"derivedFrom":subQ4}),1.0]])]});}
            var Q30;
            {var subQ5=sQuery(id+"F9.wireOp",EDGE,"E89.sketch_text.stroke-2");Q30=makeQuery(id+"F9.imprint","IMPRINT",FACE,{"disambiguationData":[TD([[makeQuery(id+"F9.imprint","IMPRINT",EDGE,{"derivedFrom":subQ5}),1.0]])]});}
            extrude(context, id + "F10", {"entities" : qUnion([Q0, Q1, Q2, Q3, Q4, Q5, Q6, Q7, Q8, Q9, Q10, Q11, Q12, Q13, Q14, Q15, Q16, Q17, Q18, Q19, Q20, Q21, Q22, Q23, Q24, Q25, Q26, Q27, Q28, Q29, Q30]), "depth" : 46.5 * mm, "hasSecondDirection" : true, "secondDirectionOppositeDirection" : false, "secondDirectionDepth" : 44.5 * mm});
        }
        {
            var Q0;
            {var subQ7=sQuery(id+"F9.wireOp",EDGE,"E65.left");Q0=makeQuery(id+"F9.imprint","IMPRINT",FACE,{"disambiguationData":[TD([[makeQuery(id+"F9.imprint","IMPRINT",EDGE,{"derivedFrom":subQ7}),-1.0]])]});}
            var Q1;
            Q1=makeQuery(id+"F9.imprint","IMPRINT",FACE,{"disambiguationData":[TD([[makeQuery(id+"F9.imprint","IMPRINT",EDGE,{"derivedFrom":sQuery(id+"F9.wireOp",EDGE,"E69")}),-1.0]])]});
            var Q2;
            {var subQ1=sQuery(id+"F9.wireOp",EDGE,"E73");Q2=makeQuery(id+"F9.imprint","IMPRINT",FACE,{"disambiguationData":[TD([[makeQuery(id+"F9.imprint","IMPRINT",EDGE,{"derivedFrom":subQ1}),1.0]])]});}
            var Q3;
            {var subQ1=sQuery(id+"F9.wireOp",EDGE,"E77");Q3=makeQuery(id+"F9.imprint","IMPRINT",FACE,{"disambiguationData":[TD([[makeQuery(id+"F9.imprint","IMPRINT",EDGE,{"derivedFrom":subQ1}),1.0]])]});}
            var Q4;
            {var subQ1=sQuery(id+"F9.wireOp",EDGE,"E75");Q4=makeQuery(id+"F9.imprint","IMPRINT",FACE,{"disambiguationData":[TD([[makeQuery(id+"F9.imprint","IMPRINT",EDGE,{"derivedFrom":subQ1}),1.0]])]});}
            var Q5;
            {var subQ10=sQuery(id+"F9.wireOp",EDGE,"E89.sketch_text.stroke-0");Q5=makeQuery(id+"F9.imprint","IMPRINT",FACE,{"disambiguationData":[TD([[makeQuery(id+"F9.imprint","IMPRINT",EDGE,{"derivedFrom":subQ10}),-1.0]])]});}
            var Q6;
            {var subQ4=sQuery(id+"F9.wireOp",EDGE,"E89.sketch_text.stroke-7");Q6=makeQuery(id+"F9.imprint","IMPRINT",FACE,{"disambiguationData":[TD([[makeQuery(id+"F9.imprint","IMPRINT",EDGE,{"derivedFrom":subQ4}),1.0]])]});}
            extrude(context, id + "F11", {"entities" : qUnion([Q0, Q1, Q2, Q3, Q4, Q5, Q6]), "operationType" : NewBodyOperationType.ADD, "depth" : 44.5 * mm, "hasSecondDirection" : true, "secondDirectionOppositeDirection" : false, "secondDirectionDepth" : 36 * mm});
        }
        {
            var Q0;
            Q0=makeQuery(id+"F2.imprint","IMPRINT",FACE,{"disambiguationData":[TD([[makeQuery(id+"F2.imprint","IMPRINT",EDGE,{"derivedFrom":sQuery(id+"F2.wireOp",EDGE,"E15.bottom")}),-1.0]])]});
            var Q1;
            Q1=makeQuery(id+"F2.imprint","IMPRINT",FACE,{"disambiguationData":[TD([[makeQuery(id+"F2.imprint","IMPRINT",EDGE,{"derivedFrom":sQuery(id+"F2.wireOp",EDGE,"E20")}),1.0]])]});
            var Q2;
            Q2=makeQuery(id+"F2.imprint","IMPRINT",FACE,{"disambiguationData":[TD([[makeQuery(id+"F2.imprint","IMPRINT",EDGE,{"derivedFrom":sQuery(id+"F2.wireOp",EDGE,"E19")}),1.0]])]});
            var Q3;
            Q3=makeQuery(id+"F2.imprint","IMPRINT",FACE,{"disambiguationData":[TD([[makeQuery(id+"F2.imprint","IMPRINT",EDGE,{"derivedFrom":sQuery(id+"F2.wireOp",EDGE,"E18")}),1.0]])]});
            var Q4;
            Q4=makeQuery(id+"F2.imprint","IMPRINT",FACE,{"disambiguationData":[TD([[makeQuery(id+"F2.imprint","IMPRINT",EDGE,{"derivedFrom":sQuery(id+"F2.wireOp",EDGE,"E17")}),1.0]])]});
            var Q5;
            Q5=makeQuery(id+"F2.imprint","IMPRINT",FACE,{"disambiguationData":[TD([[makeQuery(id+"F2.imprint","IMPRINT",EDGE,{"derivedFrom":sQuery(id+"F2.wireOp",EDGE,"E16")}),1.0]])]});
            var Q6;
            Q6=makeQuery(id+"F2.imprint","IMPRINT",FACE,{"disambiguationData":[TD([[makeQuery(id+"F2.imprint","IMPRINT",EDGE,{"derivedFrom":sQuery(id+"F2.wireOp",EDGE,"E21")}),1.0]])]});
            var Q7;
            Q7=makeQuery(id+"F2.imprint","IMPRINT",FACE,{"disambiguationData":[TD([[makeQuery(id+"F2.imprint","IMPRINT",EDGE,{"derivedFrom":sQuery(id+"F2.wireOp",EDGE,"E22")}),1.0]])]});
            extrude(context, id + "F12", {"entities" : qUnion([Q0, Q1, Q2, Q3, Q4, Q5, Q6, Q7]), "operationType" : NewBodyOperationType.REMOVE, "endBound" : BoundingType.THROUGH_ALL, "depth" : 25 * mm});
        }
        {
            var Q0;
            Q0=makeQuery(id+"F9.imprint","IMPRINT",FACE,{"disambiguationData":[TD([[makeQuery(id+"F9.imprint","IMPRINT",EDGE,{"derivedFrom":sQuery(id+"F9.wireOp",EDGE,"E88.sketch_text.stroke-0")}),-1.0]])]});
            var Q1;
            Q1=makeQuery(id+"F9.imprint","IMPRINT",FACE,{"disambiguationData":[TD([[makeQuery(id+"F9.imprint","IMPRINT",EDGE,{"derivedFrom":sQuery(id+"F9.wireOp",EDGE,"E91.sketch_text.stroke-0")}),-1.0]])]});
            var Q2;
            Q2=makeQuery(id+"F9.imprint","IMPRINT",FACE,{"disambiguationData":[TD([[makeQuery(id+"F9.imprint","IMPRINT",EDGE,{"derivedFrom":sQuery(id+"F9.wireOp",EDGE,"E90.sketch_text.stroke-0")}),-1.0]])]});
            var Q3;
            {var subQ10=sQuery(id+"F9.wireOp",EDGE,"E89.sketch_text.stroke-0");Q3=makeQuery(id+"F9.imprint","IMPRINT",FACE,{"disambiguationData":[TD([[makeQuery(id+"F9.imprint","IMPRINT",EDGE,{"derivedFrom":subQ10}),-1.0]])]});}
            var Q4;
            {var subQ1=sQuery(id+"F9.wireOp",EDGE,"E89.sketch_text.stroke-4");Q4=makeQuery(id+"F9.imprint","IMPRINT",FACE,{"disambiguationData":[TD([[makeQuery(id+"F9.imprint","IMPRINT",EDGE,{"derivedFrom":subQ1}),-1.0]])]});}
            var Q5;
            {var subQ0=sQuery(id+"F9.wireOp",EDGE,"E89.sketch_text.stroke-2");Q5=makeQuery(id+"F9.imprint","IMPRINT",FACE,{"disambiguationData":[TD([[makeQuery(id+"F9.imprint","IMPRINT",EDGE,{"derivedFrom":subQ0}),-1.0]])]});}
            var Q6;
            Q6=makeQuery(id+"F9.imprint","IMPRINT",FACE,{"disambiguationData":[TD([[makeQuery(id+"F9.imprint","IMPRINT",EDGE,{"derivedFrom":sQuery(id+"F9.wireOp",EDGE,"E86.sketch_text.stroke-0")}),-1.0]])]});
            var Q7;
            Q7=makeQuery(id+"F9.imprint","IMPRINT",FACE,{"disambiguationData":[TD([[makeQuery(id+"F9.imprint","IMPRINT",EDGE,{"derivedFrom":sQuery(id+"F9.wireOp",EDGE,"E86.sketch_text.stroke-28")}),-1.0]])]});
            var Q8;
            Q8=makeQuery(id+"F9.imprint","IMPRINT",FACE,{"disambiguationData":[TD([[makeQuery(id+"F9.imprint","IMPRINT",EDGE,{"derivedFrom":sQuery(id+"F9.wireOp",EDGE,"E86.sketch_text.stroke-40")}),-1.0]])]});
            var Q9;
            Q9=makeQuery(id+"F9.imprint","IMPRINT",FACE,{"disambiguationData":[TD([[makeQuery(id+"F9.imprint","IMPRINT",EDGE,{"derivedFrom":sQuery(id+"F9.wireOp",EDGE,"E86.sketch_text.stroke-46")}),-1.0]])]});
            var Q10;
            Q10=makeQuery(id+"F9.imprint","IMPRINT",FACE,{"disambiguationData":[TD([[makeQuery(id+"F9.imprint","IMPRINT",EDGE,{"derivedFrom":sQuery(id+"F9.wireOp",EDGE,"E86.sketch_text.stroke-58")}),-1.0]])]});
            var Q11;
            Q11=makeQuery(id+"F9.imprint","IMPRINT",FACE,{"disambiguationData":[TD([[makeQuery(id+"F9.imprint","IMPRINT",EDGE,{"derivedFrom":sQuery(id+"F9.wireOp",EDGE,"E86.sketch_text.stroke-73")}),-1.0]])]});
            var Q12;
            Q12=makeQuery(id+"F9.imprint","IMPRINT",FACE,{"disambiguationData":[TD([[makeQuery(id+"F9.imprint","IMPRINT",EDGE,{"derivedFrom":sQuery(id+"F9.wireOp",EDGE,"E85.sketch_text.stroke-0")}),-1.0]])]});
            var Q13;
            Q13=makeQuery(id+"F9.imprint","IMPRINT",FACE,{"disambiguationData":[TD([[makeQuery(id+"F9.imprint","IMPRINT",EDGE,{"derivedFrom":sQuery(id+"F9.wireOp",EDGE,"E85.sketch_text.stroke-19")}),-1.0]])]});
            var Q14;
            Q14=makeQuery(id+"F9.imprint","IMPRINT",FACE,{"disambiguationData":[TD([[makeQuery(id+"F9.imprint","IMPRINT",EDGE,{"derivedFrom":sQuery(id+"F9.wireOp",EDGE,"E85.sketch_text.stroke-31")}),-1.0]])]});
            var Q15;
            Q15=makeQuery(id+"F9.imprint","IMPRINT",FACE,{"disambiguationData":[TD([[makeQuery(id+"F9.imprint","IMPRINT",EDGE,{"derivedFrom":sQuery(id+"F9.wireOp",EDGE,"E85.sketch_text.stroke-59")}),-1.0]])]});
            var Q16;
            Q16=makeQuery(id+"F9.imprint","IMPRINT",FACE,{"disambiguationData":[TD([[makeQuery(id+"F9.imprint","IMPRINT",EDGE,{"derivedFrom":sQuery(id+"F9.wireOp",EDGE,"E85.sketch_text.stroke-71")}),-1.0]])]});
            extrude(context, id + "F13", {"entities" : qUnion([Q0, Q1, Q2, Q3, Q4, Q5, Q6, Q7, Q8, Q9, Q10, Q11, Q12, Q13, Q14, Q15, Q16]), "operationType" : NewBodyOperationType.REMOVE, "depth" : 46.5 * mm, "hasSecondDirection" : true, "secondDirectionOppositeDirection" : false, "secondDirectionDepth" : 46 * mm});
        }
        {
            var Q0;
            Q0=qCreatedBy(makeId("Top.planeOp"),FACE);
            var sketch = newSketch(context, id + "F14", { "sketchPlane" : qUnion([Q0])});
            skCircle(sketch, "E92", {"center": v(-41.18, 49.28) * mm, "radius": 2.75 * mm});
            skCircle(sketch, "E93", {"center": v(-41.18, 49.28) * mm, "radius": 1.75 * mm});
            skSolve(sketch);
        }
        {
            var Q0;
            Q0=makeQuery(id+"F14.imprint","IMPRINT",FACE,{"disambiguationData":[TD([[makeQuery(id+"F14.imprint","IMPRINT",EDGE,{"derivedFrom":sQuery(id+"F14.wireOp",EDGE,"E93")}),1.0]])]});
            var Q1;
            Q1=makeQuery(id+"F14.imprint","IMPRINT",FACE,{"disambiguationData":[TD([[makeQuery(id+"F14.imprint","IMPRINT",EDGE,{"derivedFrom":sQuery(id+"F14.wireOp",EDGE,"E92")}),1.0]])]});
            extrude(context, id + "F15", {"entities" : qUnion([Q0, Q1]), "depth" : 7 * mm});
        }
        {
            var Q0;
            Q0=makeQuery(id+"F14.imprint","IMPRINT",FACE,{"disambiguationData":[TD([[makeQuery(id+"F14.imprint","IMPRINT",EDGE,{"derivedFrom":sQuery(id+"F14.wireOp",EDGE,"E93")}),1.0]])]});
            extrude(context, id + "F16", {"entities" : qUnion([Q0]), "operationType" : NewBodyOperationType.ADD, "depth" : 11.5 * mm});
        }
    });
